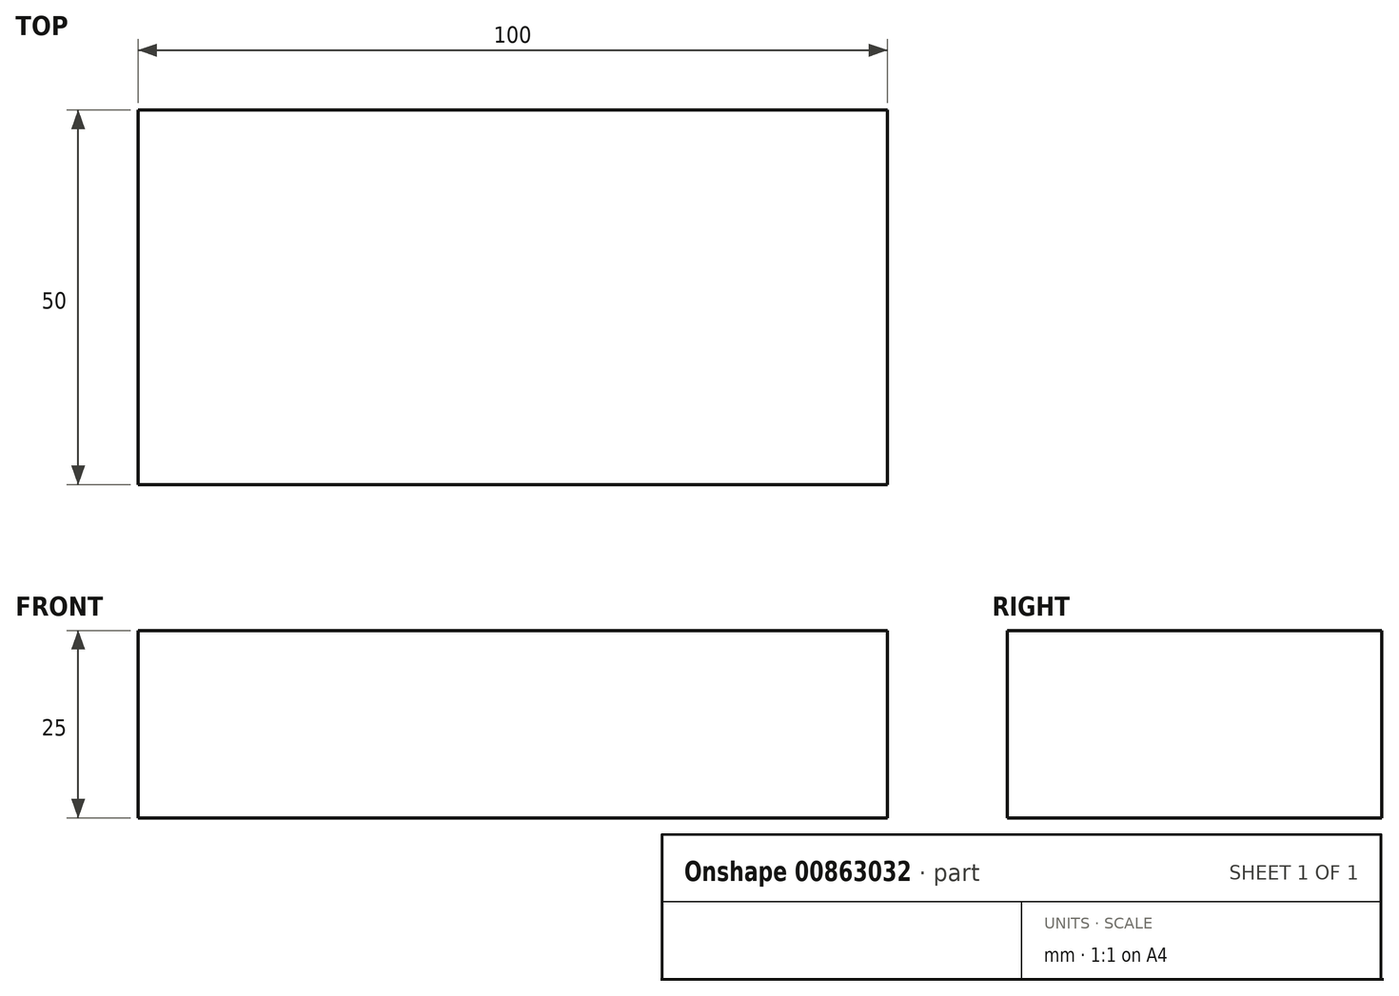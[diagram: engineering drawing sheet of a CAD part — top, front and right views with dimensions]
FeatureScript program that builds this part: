
annotation { "Feature Type Name" : "Feature", "Feature Type Description" : "" }
export const myFeature = defineFeature(function(context is Context, id is Id, definition is map)
    precondition{}
    {
        {
            var Q0;
            Q0=qCreatedBy(makeId("Top.planeOp"),FACE);
            var sketch = newSketch(context, id + "F0", { "sketchPlane" : qUnion([Q0])});
            skLineSegment(sketch, "E0.bottom", {"start": v(-50, 25) * mm, "end": v(50, 25) * mm});
            skLineSegment(sketch, "E0.top", {"start": v(-50, -25) * mm, "end": v(50, -25) * mm});
            skLineSegment(sketch, "E0.left", {"start": v(-50, 25) * mm, "end": v(-50, -25) * mm});
            skLineSegment(sketch, "E0.right", {"start": v(50, 25) * mm, "end": v(50, -25) * mm});
            skPoint(sketch, "E0.middle", {"position": v(0, 0) * mm});
            skSolve(sketch);
        }
        {
            var Q0;
            Q0 = qSketchRegion(id + "F0", true);
            extrude(context, id + "F1", {"entities" : qUnion([Q0]), "depth" : 25 * mm, "offsetDistance" : 25 * mm});
        }
        {
            var Q0;
            Q0=makeQuery(id+"F1.opExtrude","CAP_FACE",FACE,{"disambiguationData":[OSD([sQuery(id+"F0.wireOp",EDGE,"E0.bottom"),sQuery(id+"F0.wireOp",EDGE,"E0.top"),sQuery(id+"F0.wireOp",EDGE,"E0.left"),sQuery(id+"F0.wireOp",EDGE,"E0.right")])],"isStart":false});
            var sketch = newSketch(context, id + "F2", { "sketchPlane" : qUnion([Q0])});
            skArc(sketch, "E1", {"start": v(0, 12.5) * mm, "mid": v(-12.5, 0) * mm, "end": v(0, -12.5) * mm});
            skLineSegment(sketch, "E2", {"start": v(0, 12.5) * mm, "end": v(0, -12.5) * mm});
            skSolve(sketch);
        }
    });
